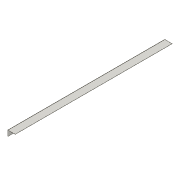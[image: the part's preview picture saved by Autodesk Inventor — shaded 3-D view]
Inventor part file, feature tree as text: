
AUTODESK INVENTOR PART (.ipt)
format: ipt  version: 2018 (Build 220112000, 112)  size: 87,040 bytes
history: native  units: in
note: dims shown in document units (in); Inventor stores cm internally (conversion verified against a paired STEP export)
features: extrude x2, sketch x2
ambient origin geometry x8: Origin, YZ Plane, XZ Plane, XY Plane, X Axis, Y Axis, Z Axis, Center Point
bodies: Solid1 (feature_tree)
feature tree (4):
  extrude  "Extrusion1"  Depth=3.0in
  extrude  "Extrusion3"  Depth=0.0747in
  sketch  "Sketch1"  dims[d0=4.0in d1=3.0in]
  sketch  "Sketch2"  dims[d2=0.0747in d3=0.0747in d4=85.0in d5=0.0in d9=15.0deg d10=1.0in d11=0.0in]
